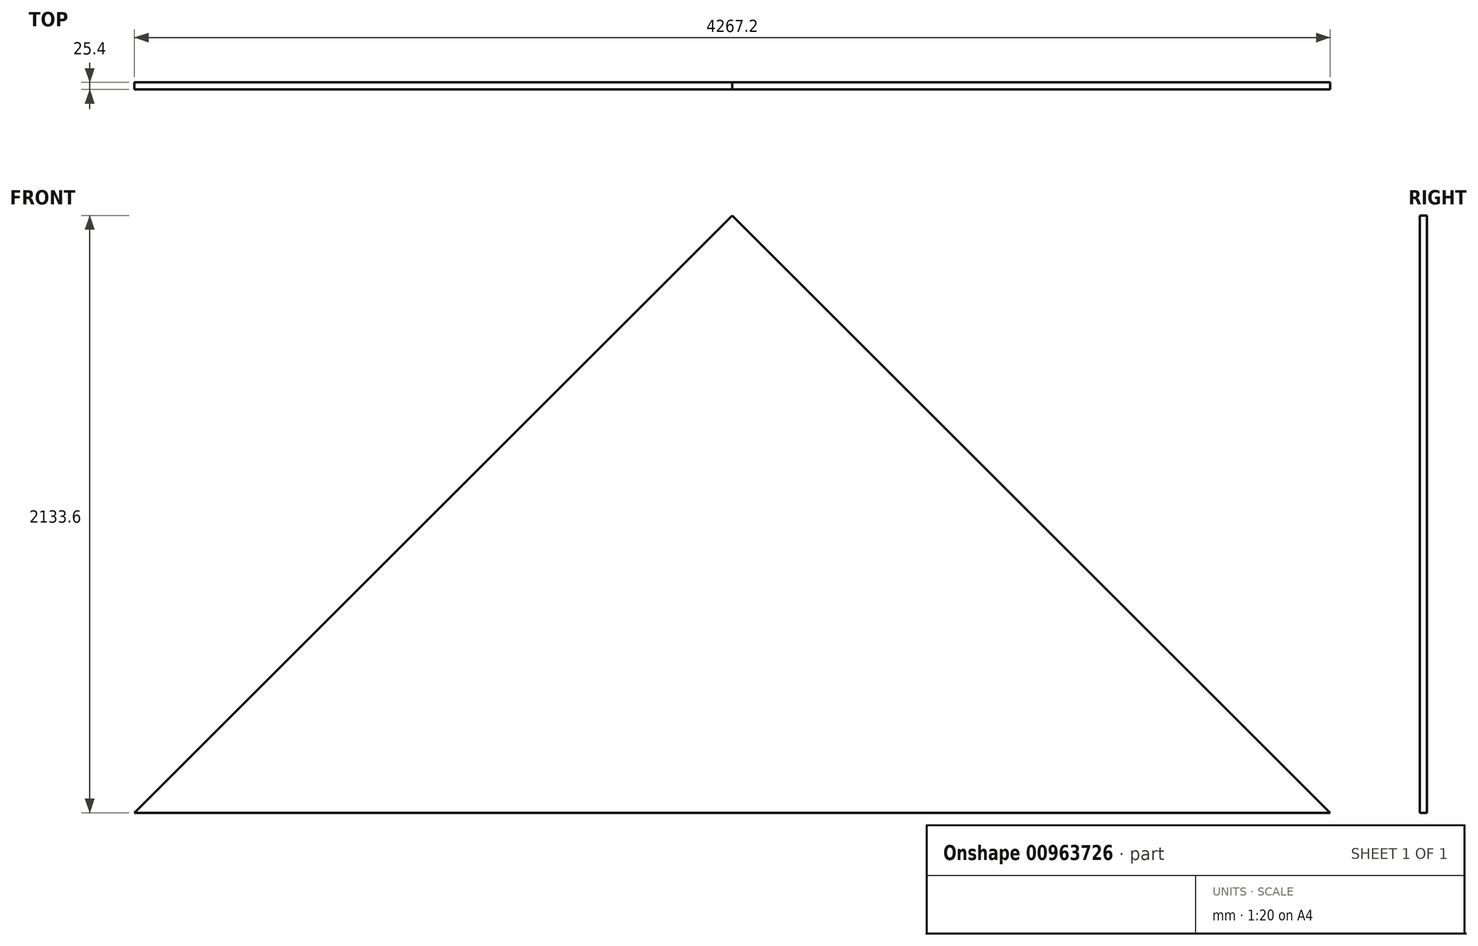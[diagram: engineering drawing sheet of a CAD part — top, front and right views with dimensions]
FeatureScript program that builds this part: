
annotation { "Feature Type Name" : "Feature", "Feature Type Description" : "" }
export const myFeature = defineFeature(function(context is Context, id is Id, definition is map)
    precondition{}
    {
        {
            var Q0;
            Q0=qCreatedBy(makeId("Front.planeOp"),FACE);
            var sketch = newSketch(context, id + "F0", { "sketchPlane" : qUnion([Q0])});
            skLineSegment(sketch, "E0", {"start": v(0, 0) * mm, "end": v(2133.6, 0) * mm});
            skLineSegment(sketch, "E1", {"start": v(2133.6, 0) * mm, "end": v(0, 2133.6) * mm});
            skLineSegment(sketch, "E2", {"start": v(0, 2133.6) * mm, "end": v(-2133.6, 0) * mm});
            skLineSegment(sketch, "E3", {"start": v(-2133.6, 0) * mm, "end": v(0, 0) * mm});
            skSolve(sketch);
        }
        {
            var Q0;
            Q0=makeQuery(id+"F0.imprint","IMPRINT",FACE,{"disambiguationData":[TD([[makeQuery(id+"F0.imprint","IMPRINT",EDGE,{"derivedFrom":sQuery(id+"F0.wireOp",EDGE,"E0")}),1.0]])]});
            extrude(context, id + "F1", {"entities" : qUnion([Q0]), "depth" : 25.4 * mm, "offsetDistance" : 25.4 * mm});
        }
    });
